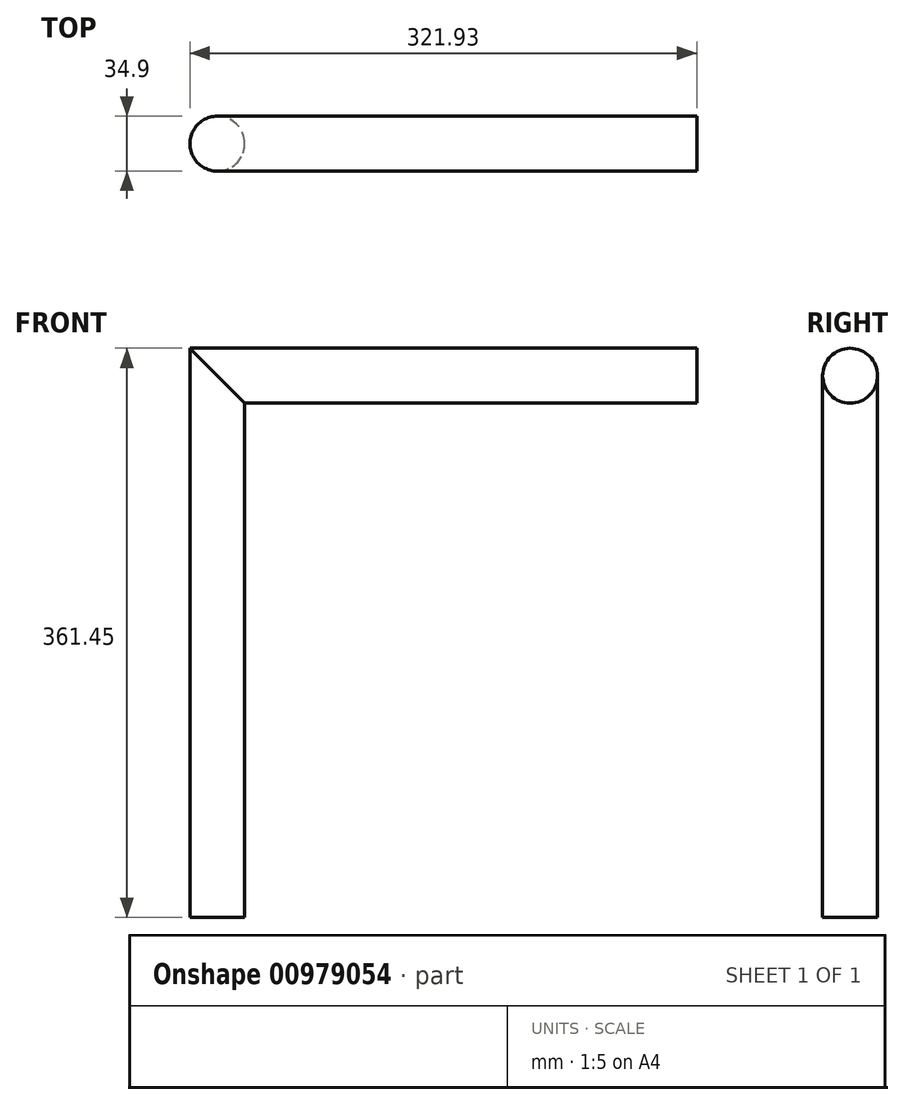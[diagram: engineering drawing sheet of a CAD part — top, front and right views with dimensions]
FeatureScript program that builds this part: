
annotation { "Feature Type Name" : "Feature", "Feature Type Description" : "" }
export const myFeature = defineFeature(function(context is Context, id is Id, definition is map)
    precondition{}
    {
        {
            var Q0;
            Q0=qCreatedBy(makeId("Top.planeOp"),FACE);
            var sketch = newSketch(context, id + "F0", { "sketchPlane" : qUnion([Q0])});
            skCircle(sketch, "E0", {"center": v(-0.1, 0.1) * mm, "radius": 17.45 * mm});
            skSolve(sketch);
        }
        {
            var Q0;
            Q0=qCreatedBy(makeId("Front.planeOp"),FACE);
            var sketch = newSketch(context, id + "F1", { "sketchPlane" : qUnion([Q0])});
            skLineSegment(sketch, "E1", {"start": v(0, 0) * mm, "end": v(0, 343.91) * mm});
            skLineSegment(sketch, "E2", {"start": v(0, 343.91) * mm, "end": v(304.39, 343.91) * mm});
            skSolve(sketch);
        }
        {
            var Q0;
            Q0=makeQuery(id+"F0.imprint","IMPRINT",FACE,{"disambiguationData":[TD([[makeQuery(id+"F0.imprint","IMPRINT",EDGE,{"derivedFrom":sQuery(id+"F0.wireOp",EDGE,"E0")}),1.0]])]});
            var Q1;
            Q1=sQuery(id+"F1.wireOp",EDGE,"E2");
            var Q2;
            Q2=sQuery(id+"F1.wireOp",EDGE,"E1");
            sweep(context, id + "F2", {"profiles" : qUnion([Q0]), "path" : qUnion([Q1, Q2])});
        }
    });
